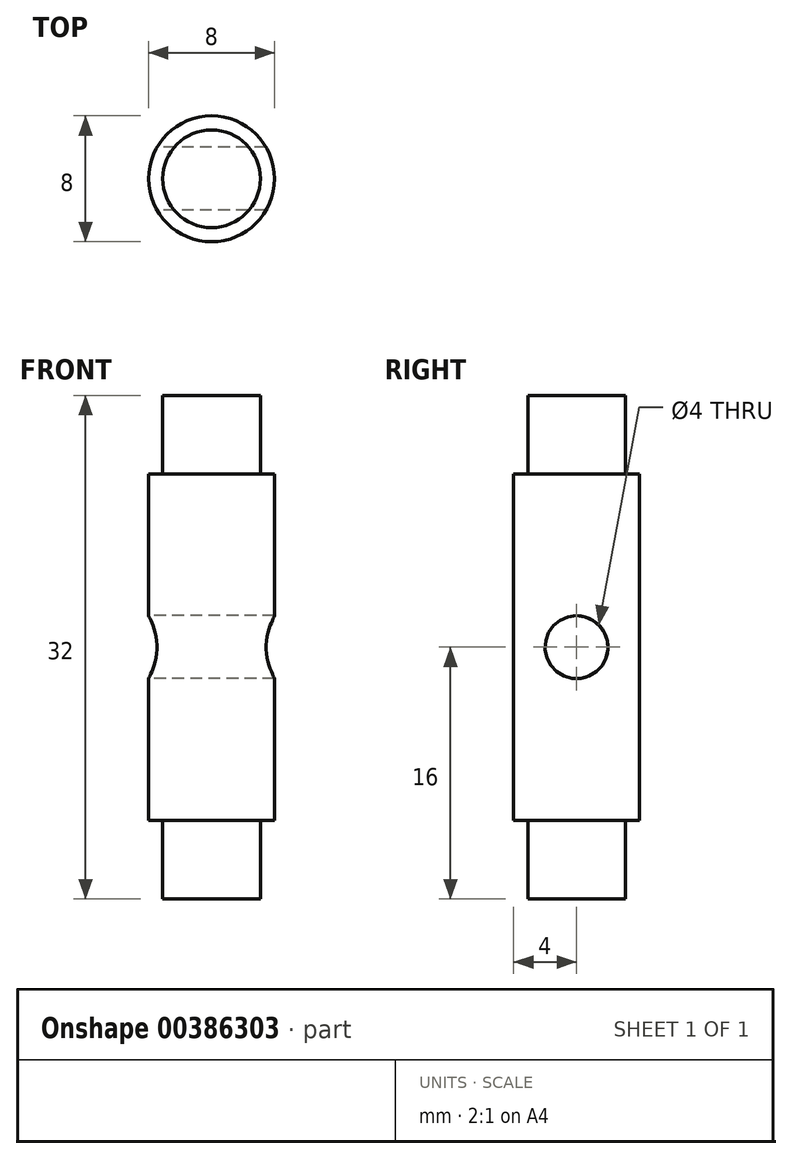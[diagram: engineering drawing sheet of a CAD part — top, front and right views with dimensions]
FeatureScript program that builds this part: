
annotation { "Feature Type Name" : "Feature", "Feature Type Description" : "" }
export const myFeature = defineFeature(function(context is Context, id is Id, definition is map)
    precondition{}
    {
        {
            var Q0;
            Q0=qCreatedBy(makeId("Top.planeOp"),FACE);
            var sketch = newSketch(context, id + "F0", { "sketchPlane" : qUnion([Q0])});
            skCircle(sketch, "E0", {"center": v(0, 0) * mm, "radius": 4 * mm});
            skCircle(sketch, "E1", {"center": v(0, 0) * mm, "radius": 3.1 * mm});
            skSolve(sketch);
        }
        {
            var Q0;
            Q0=makeQuery(id+"F0.imprint","IMPRINT",FACE,{"disambiguationData":[TD([[makeQuery(id+"F0.imprint","IMPRINT",EDGE,{"derivedFrom":sQuery(id+"F0.wireOp",EDGE,"E0")}),1.0]])]});
            extrude(context, id + "F1", {"entities" : qUnion([Q0]), "depth" : 22 * mm});
        }
        {
            var Q0;
            Q0=makeQuery(id+"F0.imprint","IMPRINT",FACE,{"disambiguationData":[TD([[makeQuery(id+"F0.imprint","IMPRINT",EDGE,{"derivedFrom":sQuery(id+"F0.wireOp",EDGE,"E1")}),1.0]])]});
            extrude(context, id + "F2", {"entities" : qUnion([Q0]), "operationType" : NewBodyOperationType.ADD, "depth" : 27 * mm});
        }
        {
            var Q0;
            Q0=makeQuery(id+"F0.imprint","IMPRINT",FACE,{"disambiguationData":[TD([[makeQuery(id+"F0.imprint","IMPRINT",EDGE,{"derivedFrom":sQuery(id+"F0.wireOp",EDGE,"E1")}),1.0]])]});
            extrude(context, id + "F3", {"entities" : qUnion([Q0]), "operationType" : NewBodyOperationType.ADD, "oppositeDirection" : true, "depth" : 5 * mm});
        }
        {
            var Q0;
            Q0=qCreatedBy(makeId("Right.planeOp"),FACE);
            var sketch = newSketch(context, id + "F4", { "sketchPlane" : qUnion([Q0])});
            skLineSegment(sketch, "E2", {"start": v(0, 0) * mm, "end": v(0, 45.02) * mm});
            skCircle(sketch, "E3", {"center": v(0, 11) * mm, "radius": 2 * mm});
            skSolve(sketch);
        }
        {
            var Q0;
            Q0=qSketchRegion(id+"F4",true);
            extrude(context, id + "F5", {"entities" : qUnion([Q0]), "operationType" : NewBodyOperationType.REMOVE, "depth" : 25 * mm});
        }
        {
            var Q0;
            Q0=makeQuery(id+"F5.boolean.opBoolean","COPY",FACE,{"derivedFrom":makeQuery(id+"F5.opExtrude","CAP_FACE",FACE,{"disambiguationData":[OSD([sQuery(id+"F4.wireOp",EDGE,"E3")])],"isStart":true})});
            extrude(context, id + "F6", {"entities" : qUnion([Q0]), "operationType" : NewBodyOperationType.REMOVE, "oppositeDirection" : true, "depth" : 25 * mm});
        }
    });
